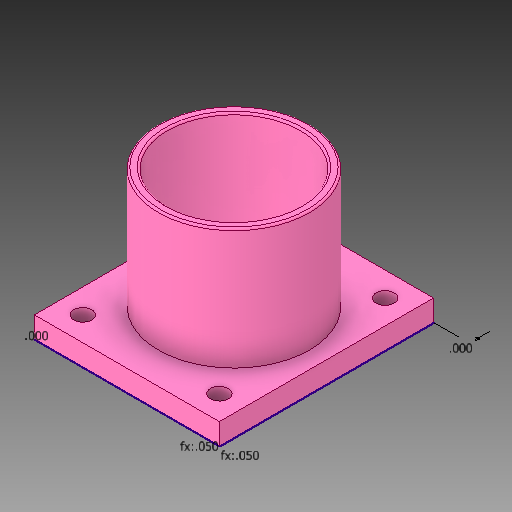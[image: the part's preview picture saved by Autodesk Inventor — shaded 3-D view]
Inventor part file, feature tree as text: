
AUTODESK INVENTOR PART (.ipt)
format: ipt  version: 2019.3 (Build 233278000, 278)  size: 215,552 bytes
history: native  units: in
note: dims shown in document units (in); Inventor stores cm internally (conversion verified against a paired STEP export)
features: sketch x5, extrude x3, fillet x3, hole x1, chamfer x1
ambient origin geometry x8: Origin, YZ Plane, XZ Plane, XY Plane, X Axis, Y Axis, Z Axis, Center Point
bodies: Solid1 (feature_tree)
feature tree (13):
  extrude  "ExtrusionForFloor"  Depth=1.7717in
  extrude  "ExtrusionForCameraHole"  Depth=0.3937in
  sketch  "Sketch5"  dims[d22=1.0in d23=0.0in d24=0.05in]
  extrude  "ExtrusionForEyepieceAttachement"  Depth=1.0in
  hole  "Hole5"  [1 undecoded]
  fillet  "Fillet3"  Radius=1.1in
  fillet  "Fillet4"  Radius=1.0in
  fillet  "Fillet5"  Radius=0.1in
  chamfer  "Chamfer2"  [1 undecoded]
  sketch  "Sketch1"  dims[d0=1.53in d1=1.7717in]
  sketch  "Sketch4"  dims[d2=0.175in d3=0.0in d21=0.3937in]
  sketch  "Sketch7"  dims[d25=0.05in d32=1.25in d33=1.1in d34=1.0in d35=0.0in d36=0.1in]
  sketch  "Sketch19"  dims[d41=0.0in d43=0.0in d86=0.15in d87=0.75in d88=0.172in d89=0.25in d90=0.5635in d91=1.0in d92=0.8108in d95=0.0156in d96=0.0394in d97=0.0394in d101=0.125in d102=0.125in d103=45.0deg d104=0.2in d105=0.2in d106=0.2in d107=0.2in d108=0.2in d109=0.2in d110=0.2in d111=0.2in d93=0.75in d94=0.8108in]
note: 2 required parameter values undecoded (feature->parameter linkage not recoverable at this tier; creation-order binding heuristic only, values carry confidence <= 0.55)
